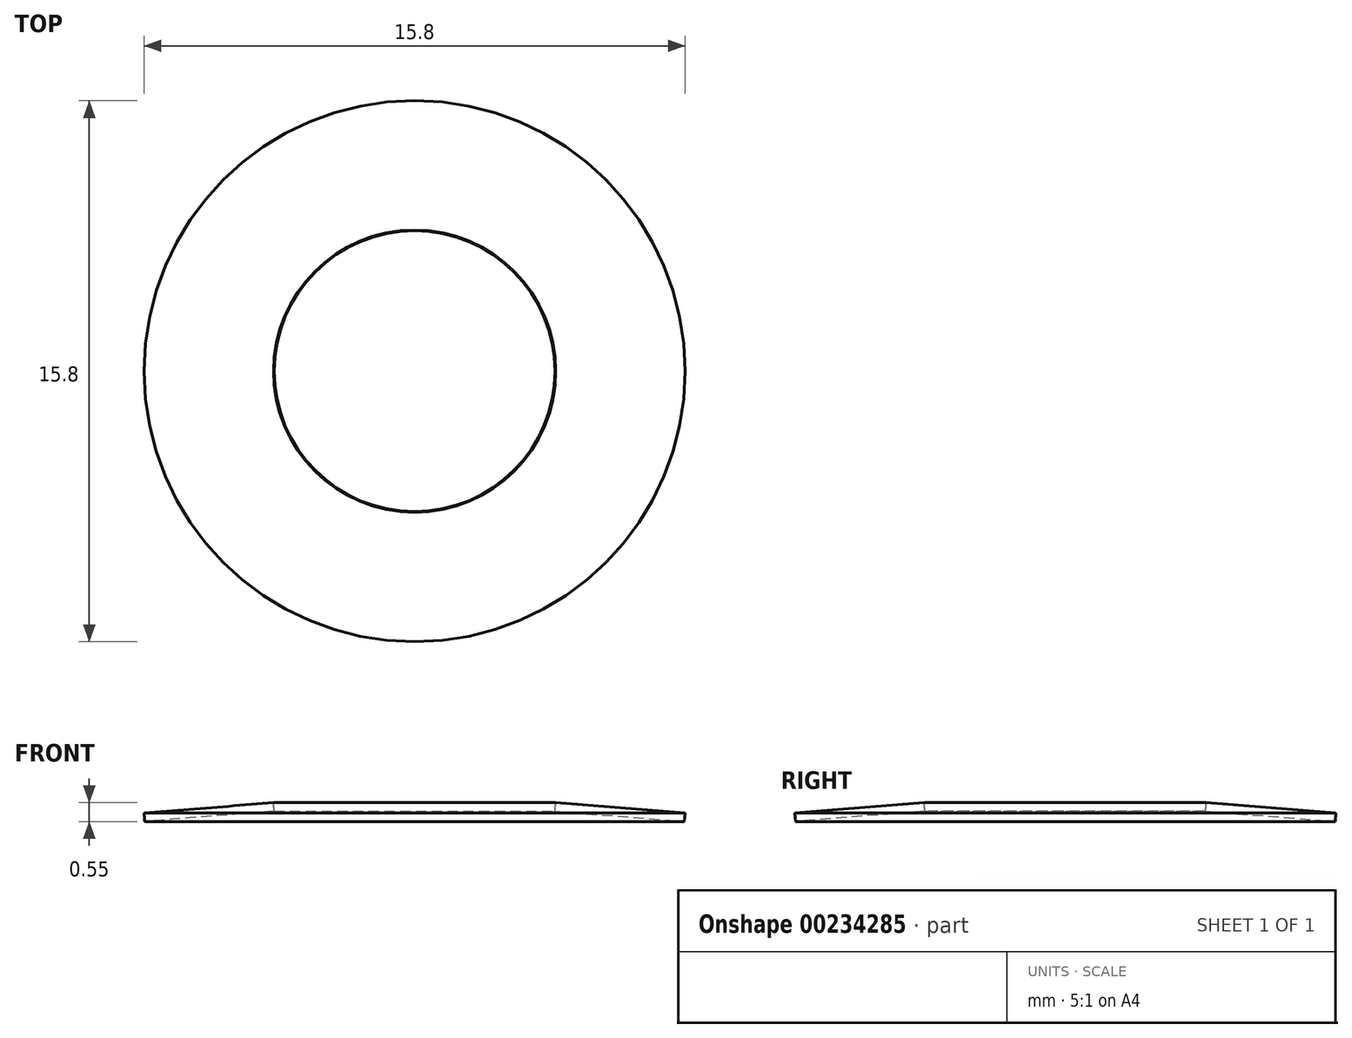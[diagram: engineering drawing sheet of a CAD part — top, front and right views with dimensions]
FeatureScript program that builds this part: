
annotation { "Feature Type Name" : "Feature", "Feature Type Description" : "" }
export const myFeature = defineFeature(function(context is Context, id is Id, definition is map)
    precondition{}
    {
        {
            var Q0;
            Q0=qCreatedBy(makeId("Front.planeOp"),FACE);
            var sketch = newSketch(context, id + "F0", { "sketchPlane" : qUnion([Q0])});
            skLineSegment(sketch, "E0", {"start": v(0, 0) * mm, "end": v(0, 8.93) * mm, "construction": true});
            skLineSegment(sketch, "E1", {"start": v(-7.88, -0.25) * mm, "end": v(-7.9, 0) * mm});
            skLineSegment(sketch, "E2", {"start": v(-7.88, -0.25) * mm, "end": v(-4.1, 0.05) * mm});
            skLineSegment(sketch, "E3", {"start": v(-4.12, 0.3) * mm, "end": v(-4.1, 0.05) * mm});
            skLineSegment(sketch, "E4", {"start": v(-4.12, 0.3) * mm, "end": v(-7.9, 0) * mm});
            skSolve(sketch);
        }
        {
            var Q0;
            Q0 = qSketchRegion(id + "F0", true);
            var Q1;
            Q1=sQuery(id+"F0.wireOp",EDGE,"E0");
            revolve(context, id + "F1", {"entities" : qUnion([Q0]), "axis" : qUnion([Q1]), "revolveType" : RevolveType.FULL});
        }
    });
